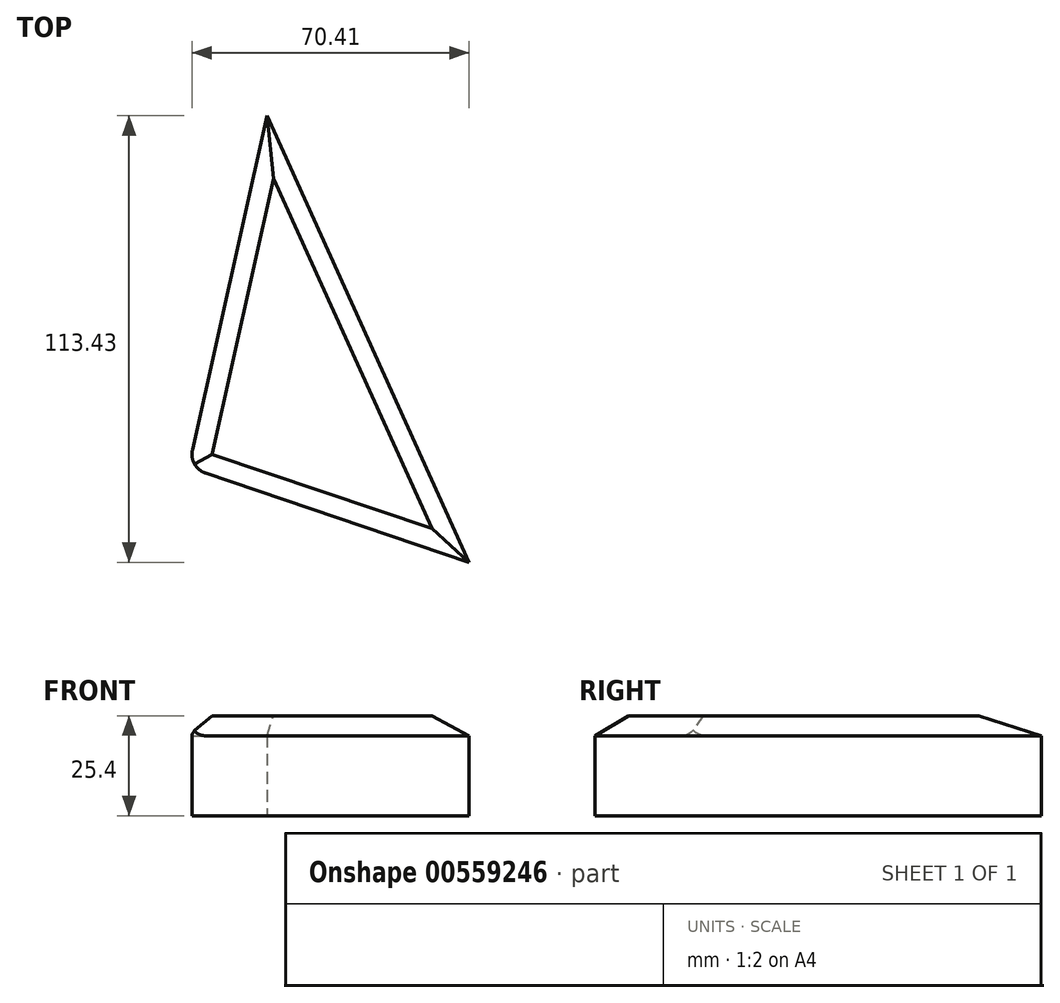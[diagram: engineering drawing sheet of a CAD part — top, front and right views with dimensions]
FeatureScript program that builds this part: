
annotation { "Feature Type Name" : "Feature", "Feature Type Description" : "" }
export const myFeature = defineFeature(function(context is Context, id is Id, definition is map)
    precondition{}
    {
        {
            var Q0;
            Q0=qCreatedBy(makeId("Top.planeOp"),FACE);
            var sketch = newSketch(context, id + "F0", { "sketchPlane" : qUnion([Q0])});
            skLineSegment(sketch, "E0", {"start": v(-77.73, -85.83) * mm, "end": v(-129.06, 27.6) * mm});
            skLineSegment(sketch, "E1", {"start": v(-149.02, -61.74) * mm, "end": v(-129.06, 27.6) * mm});
            skLineSegment(sketch, "E2", {"start": v(-149.02, -61.74) * mm, "end": v(-77.73, -85.83) * mm});
            skSolve(sketch);
        }
        {
            var Q0;
            Q0=makeQuery(id+"F0.imprint","IMPRINT",FACE,{"disambiguationData":[TD([[makeQuery(id+"F0.imprint","IMPRINT",EDGE,{"derivedFrom":sQuery(id+"F0.wireOp",EDGE,"E0")}),1.0]])]});
            extrude(context, id + "F1", {"entities" : qUnion([Q0]), "depth" : 25.4 * mm, "offsetDistance" : 25.4 * mm});
        }
        {
            var Q0;
            Q0=makeQuery(id+"F1.opExtrude","CAP_FACE",FACE,{"disambiguationData":[OSD([sQuery(id+"F0.wireOp",EDGE,"E0"),sQuery(id+"F0.wireOp",EDGE,"E1"),sQuery(id+"F0.wireOp",EDGE,"E2")])],"isStart":false});
            var Q1;
            Q1=makeQuery(id+"F1.opExtrude","CAP_EDGE",EDGE,{"disambiguationData":[OSD([sQuery(id+"F0.wireOp",EDGE,"E2")])],"isStart":false});
            var Q2;
            Q2=makeQuery(id+"F1.opExtrude","CAP_EDGE",EDGE,{"disambiguationData":[OSD([sQuery(id+"F0.wireOp",EDGE,"E1")])],"isStart":false});
            var Q3;
            Q3=makeQuery(id+"F1.opExtrude","CAP_EDGE",EDGE,{"disambiguationData":[OSD([sQuery(id+"F0.wireOp",EDGE,"E0")])],"isStart":false});
            chamfer(context, id + "F2", {"entities" : qUnion([Q0, Q1, Q2, Q3]), "width" : 5.08 * mm, "tangentPropagation" : true});
        }
        {
            var Q0;
            Q0=makeQuery(id+"F1.opExtrude","SWEPT_EDGE",EDGE,{"disambiguationData":[OSD([sQuery(id+"F0.wireOp",EDGE,"E1"),sQuery(id+"F0.wireOp",EDGE,"E2")])]});
            fillet(context, id + "F3", {"entities" : qUnion([Q0]), "radius" : 5.08 * mm, "tangentPropagation" : true, "allowEdgeOverflow" : false});
        }
    });
